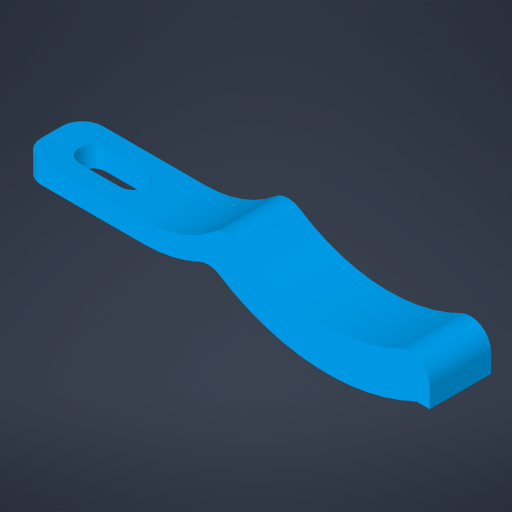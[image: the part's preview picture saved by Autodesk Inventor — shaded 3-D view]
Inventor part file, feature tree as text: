
AUTODESK INVENTOR PART (.ipt)
format: ipt  version: 2023.4 (Build 274418000, 418)  size: 247,808 bytes
history: native  units: mm
features: sketch x2, extrude x2, plane x1, fillet x1, projected_geometry x1
ambient origin geometry x8: Origin, YZ Plane, XZ Plane, XY Plane, X Axis, Y Axis, Z Axis, Center Point
bodies: Solid1 (feature_tree)
feature tree (7):
  sketch  "Sketch1"  dims[d0=45.0mm d1=10.0mm d2=20.0mm d3=2.5mm d4=5.0mm d5=10.0mm d6=9.0mm d7=2.0mm d8=2.5mm d9=1.0mm d10=1.5mm d22=50.0mm]
  plane  "Work Plane1"
  extrude  "Extrusion1"  Depth=50.0mm
  extrude  "Extrusion2"  Depth=2.5mm
  fillet  "Fillet1"  Radius=2.5mm
  sketch  "Sketch2"  dims[d23=10.0mm d24=20.0mm d25=2.5mm d26=5.0mm d27=10.0mm d28=9.0mm d29=2.0mm d30=1.0mm d31=2.5mm d32=1.0mm d33=1.5mm d34=7.5mm d35=0.0mm d36=5.0mm d37=5.0mm d38=3.25mm d39=7.5mm d40=0.0mm d41=2.5mm]
  projected_geometry  "Projected Loop1"
